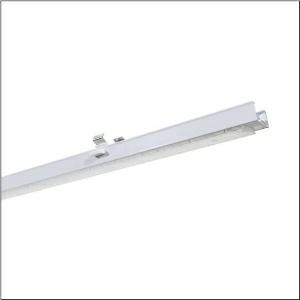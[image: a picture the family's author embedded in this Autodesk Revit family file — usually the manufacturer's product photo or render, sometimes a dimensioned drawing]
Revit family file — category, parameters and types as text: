
# Revit family: sanierungs-leuchteneinsatz_31_gen_2_51re12mb68b_ffbb
name_source: partatom
category: Lighting Fixtures
units: mm (PartAtom-declared; Revit-internal decimal feet)

## family parameters
Cut with Voids When Loaded = No
Host = Face
Light Source = No
Part Type = Normal
Room Calculation Point = No
Round Connector Dimension = Use Diameter
Shared = No

## types (1)
- --- (1 x LED, 8000 lm, 50 W, 6500K)
    Apparent Load = 50 VA
    CIE Flux Codes = 65 91 98 99 100
    Color Rendering = 80
    Color Temperature = 6500K
    Default Elevation = 1800 mm
    Description = Refurbishment luminaire insert Gen.2, luminaire insert, of extruded aluminium section, coated, traffic white (RAL 9016), length: 1.472mm, width: 91mm, height: 53mm, LED rated luminous flux: 8.000lm, light colour: 865, control gear: ON/OFF Multilumen, control gear: ECG Multilumen, with system connector: socket, mains connection: 220..240V, AC/DC, 0/50..60Hz, luminous flux adjustable on luminaire in four steps (4280/5650/6950/8270lm), connected load according to luminous flux setting (24/32/40/49W), primary light control with lens, of plastic, primary optical cover: cover, of PMMA, light emission: direct distribution, protection rating (complete): IP20, insulation class (complete): insulation class I (protective earthing), certification: CE, UKCA, permissible ambient temperature for indoor applications: -20..+40°C, packaging unit: 1 piece
    Height = 58 mm
    Lamp = 1 x LED
    Lamp Light Flux = 8000 lm
    Lamp Power = 50 W
    Lamp count = 1
    Length = 1472 mm
    Luminous efficacy = 160 lm/W
    Manufacturer = Siteco
    ModVariant = No
    Model = 51RE12MB68B
    Mounting Place = Ceiling
    Mounting Type = Pendant
    Number of Poles = 1
    OnlyDefault = Yes
    Power Factor = 1
    Product Name = Sanierungs-Leuchteneinsatz 31 Gen.2
    Product group = luminaire insert
    ProductGroupID = 902
    Protection Class = Protection class I
    Protection Degree = IP 20
    RLX_Detail_Level = 1
    RlxData = <blob elided: 20333 chars, md5=03826da8>
    Socket = socket
    Standby Power = 0 W
    System Light Flux = 8000 lm
    System Power = 50 W
    Type Comments = factory setting: luminous flux: 100 % | (ON | ON) | 300 mA
    Type Image = l_1266702.jpg
    URL = http://relux.com
    VarID = @adj_090901
    Voltage = 0 V
    Weight = 0.00 kg
    Width = 65 mm

## geometry (parser evidence)
native form markers: Blend x4, Sweep x10
no freeform markers — native parametric forms only
